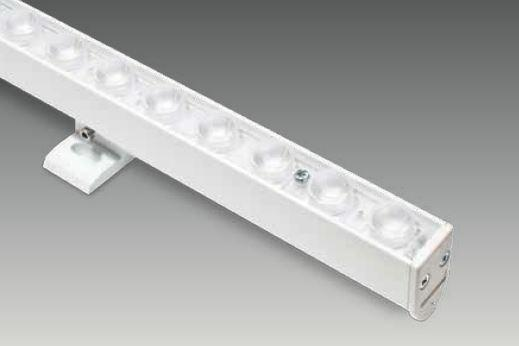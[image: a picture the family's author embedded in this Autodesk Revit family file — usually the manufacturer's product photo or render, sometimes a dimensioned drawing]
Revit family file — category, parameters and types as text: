
# Revit family: SD 0900 RUB
name_source: partatom
category: Lighting Fixtures
revit_build: Autodesk Revit 2017 (Build: 20160225_1515(x64)
units: mm (PartAtom-declared; Revit-internal decimal feet)

## family parameters
Cut with Voids When Loaded = No
Host = Face
Light Source = Yes
Part Type = Normal
Room Calculation Point = No
Round Connector Dimension = Use Diameter
Shared = No

## types (3) — shared parameters
Apparent Load = 33 VA
Color Filter = 16777215
Default Elevation = 1219 mm
Dimming Lamp Color Temperature Shift = <None>
Emit Shape Visible in Rendering = Yes
Emit from Rectangle Length = 20 mm  [stored 0.0656168 ft]
Emit from Rectangle Width = 895 mm  [stored 2.93635 ft]
Light Source Symbol Size = 610 mm
Manufacturer = ARLIGHT
Type Image = SD 0900 RUB.JPG
Wattage Comments = 33

## per-type parameters (varying)
| type | Beam Angle |
| SDRUB.900.38.33.30 | 38.00° |
| SDRUB.900.27.33.30 | 27.00° |
| SDRUB.900.4520.33.30 | 20.00° |

note: [stored X ft] marks values corroborated as IEEE doubles in the binary element streams (Revit-internal decimal feet)

## geometry (parser evidence)
native form markers: Sweep x3
no freeform markers — native parametric forms only
